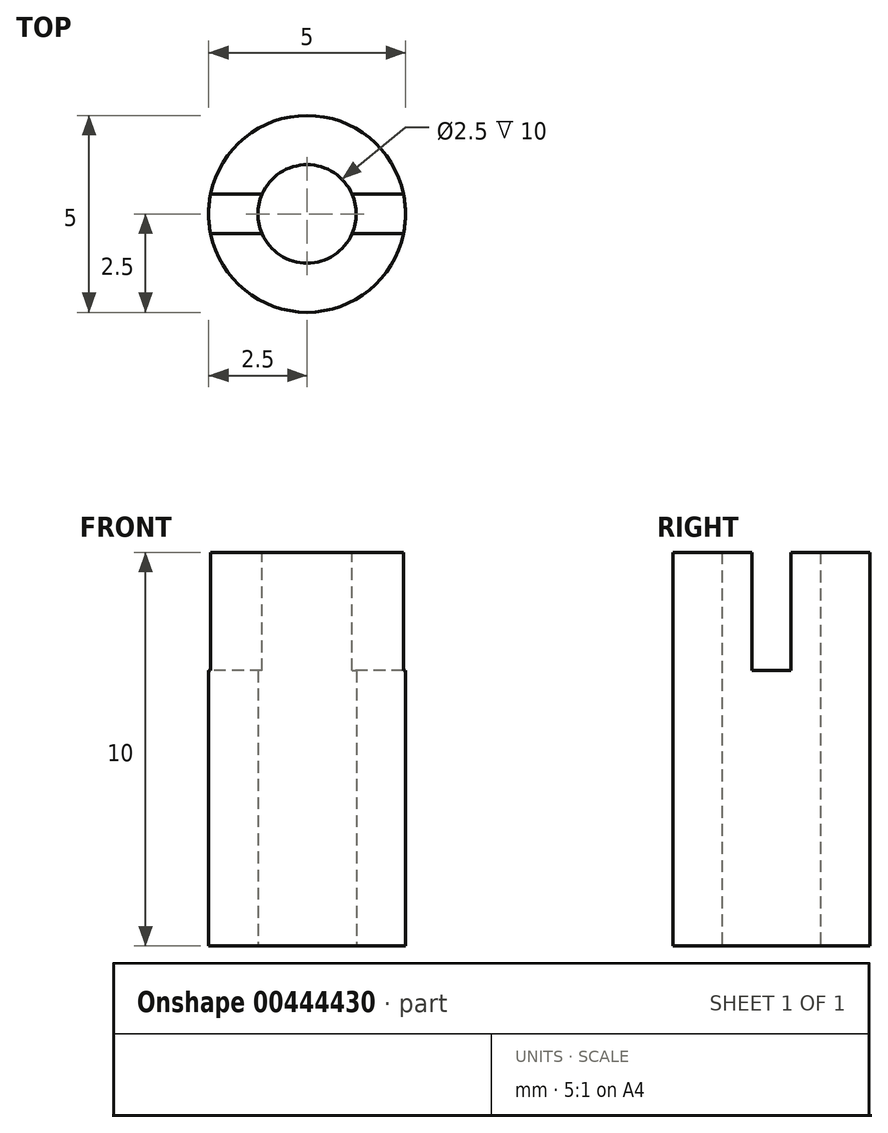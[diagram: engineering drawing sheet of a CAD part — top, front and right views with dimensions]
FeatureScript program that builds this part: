
annotation { "Feature Type Name" : "Feature", "Feature Type Description" : "" }
export const myFeature = defineFeature(function(context is Context, id is Id, definition is map)
    precondition{}
    {
        {
            var Q0;
            Q0=qCreatedBy(makeId("Top.planeOp"),FACE);
            var sketch = newSketch(context, id + "F0", { "sketchPlane" : qUnion([Q0])});
            skCircle(sketch, "E0", {"center": v(0, 0) * mm, "radius": 2.5 * mm});
            skCircle(sketch, "E1", {"center": v(0, 0) * mm, "radius": 1.25 * mm});
            skSolve(sketch);
        }
        {
            var Q0;
            Q0=makeQuery(id+"F0.imprint","IMPRINT",FACE,{"disambiguationData":[TD([[makeQuery(id+"F0.imprint","IMPRINT",EDGE,{"derivedFrom":sQuery(id+"F0.wireOp",EDGE,"E0")}),1.0]])]});
            extrude(context, id + "F1", {"entities" : qUnion([Q0]), "depth" : 10 * mm});
        }
        {
            var Q0;
            Q0=makeQuery(id+"F1.opExtrude","CAP_FACE",FACE,{"disambiguationData":[OSD([sQuery(id+"F0.wireOp",EDGE,"E0"),sQuery(id+"F0.wireOp",EDGE,"E1")])],"isStart":false});
            var sketch = newSketch(context, id + "F2", { "sketchPlane" : qUnion([Q0])});
            skLineSegment(sketch, "E2.bottom", {"start": v(3.1, 0.5) * mm, "end": v(-3.1, 0.5) * mm});
            skLineSegment(sketch, "E2.top", {"start": v(3.1, -0.5) * mm, "end": v(-3.1, -0.5) * mm});
            skLineSegment(sketch, "E2.left", {"start": v(3.1, 0.5) * mm, "end": v(3.1, -0.5) * mm});
            skLineSegment(sketch, "E2.right", {"start": v(-3.1, 0.5) * mm, "end": v(-3.1, -0.5) * mm});
            skPoint(sketch, "E2.middle", {"position": v(0, 0) * mm});
            skSolve(sketch);
        }
        {
            var Q0;
            {var subQ0=sQuery(id+"F2.wireOp",EDGE,"E2.bottom");var subQ1=makeQuery(id+"F1.opExtrude","CAP_EDGE",EDGE,{"disambiguationData":[OSD([sQuery(id+"F0.wireOp",EDGE,"E0")])],"isStart":false});var subQ2=makeQuery(id+"F2.imprint","INTERSECT",VERTEX,{"disambiguationData":[OD(1.0)],"derivedFrom":[subQ1,subQ0]});Q0=makeQuery(id+"F2.imprint","IMPRINT",FACE,{"disambiguationData":[TD([[makeQuery(id+"F2.imprint","IMPRINT",EDGE,{"disambiguationData":[TD([[subQ2,1.0]])],"derivedFrom":subQ0}),1.0]])]});}
            var Q1;
            {var subQ0=sQuery(id+"F2.wireOp",EDGE,"E2.bottom");var subQ1=makeQuery(id+"F1.opExtrude","CAP_EDGE",EDGE,{"disambiguationData":[OSD([sQuery(id+"F0.wireOp",EDGE,"E0")])],"isStart":false});var subQ2=makeQuery(id+"F2.imprint","INTERSECT",VERTEX,{"disambiguationData":[OD(0.0)],"derivedFrom":[subQ1,subQ0]});Q1=makeQuery(id+"F2.imprint","IMPRINT",FACE,{"disambiguationData":[TD([[makeQuery(id+"F2.imprint","IMPRINT",EDGE,{"disambiguationData":[TD([[subQ2,-1.0]])],"derivedFrom":subQ0}),1.0]])]});}
            extrude(context, id + "F3", {"entities" : qUnion([Q0, Q1]), "operationType" : NewBodyOperationType.REMOVE, "oppositeDirection" : true, "depth" : 3 * mm});
        }
    });
